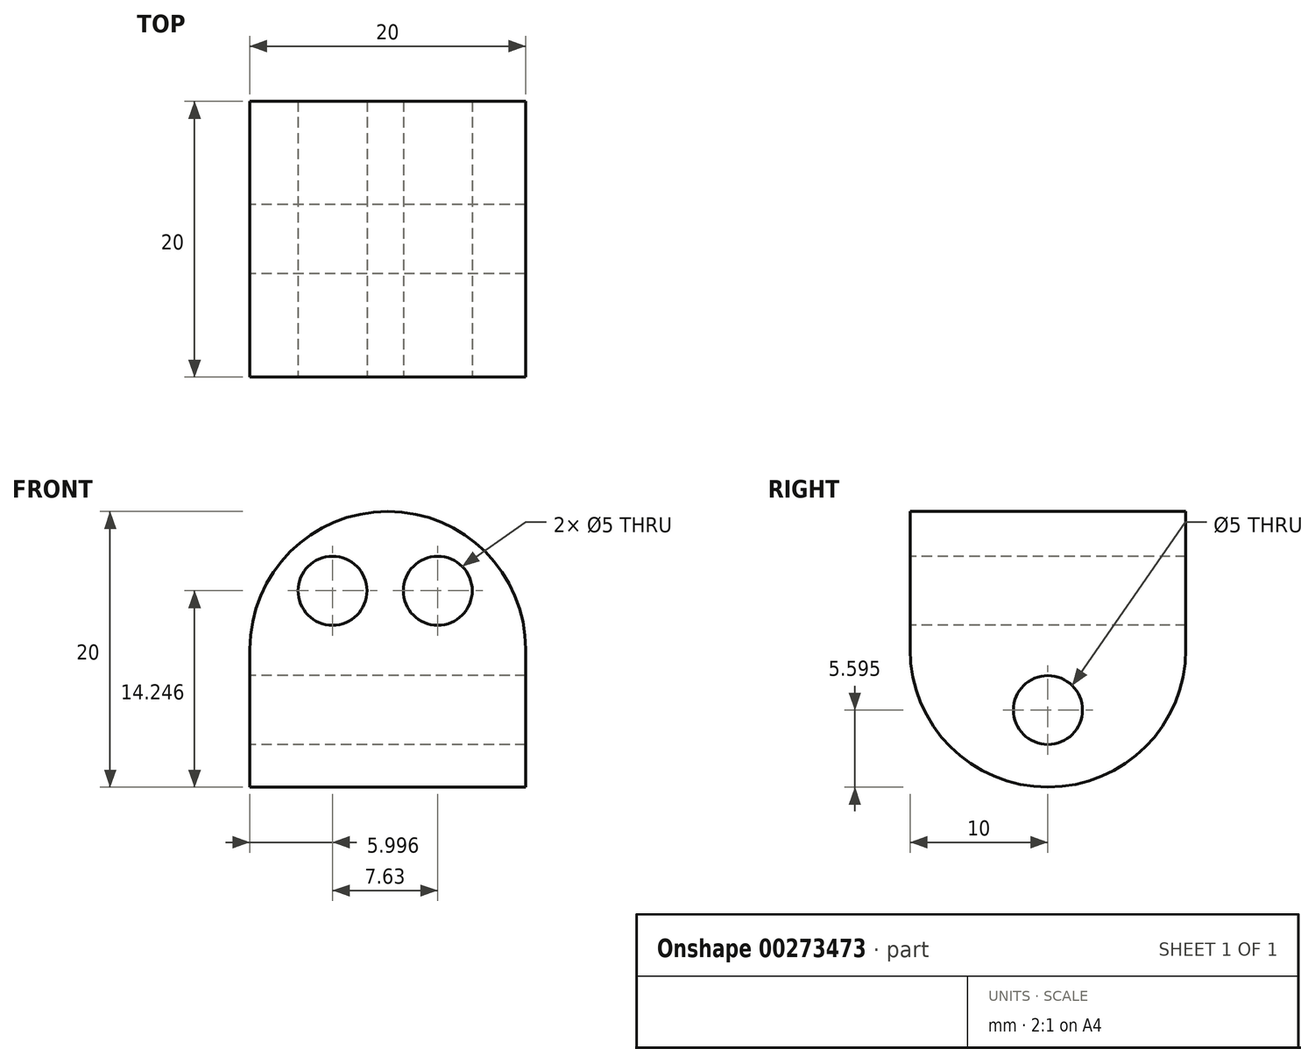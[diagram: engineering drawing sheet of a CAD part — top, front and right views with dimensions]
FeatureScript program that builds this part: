
annotation { "Feature Type Name" : "Feature", "Feature Type Description" : "" }
export const myFeature = defineFeature(function(context is Context, id is Id, definition is map)
    precondition{}
    {
        {
            var Q0;
            Q0=qCreatedBy(makeId("Top.planeOp"),FACE);
            var sketch = newSketch(context, id + "F0", { "sketchPlane" : qUnion([Q0])});
            skLineSegment(sketch, "E0.bottom", {"start": v(10, 10) * mm, "end": v(-10, 10) * mm});
            skLineSegment(sketch, "E0.top", {"start": v(10, -10) * mm, "end": v(-10, -10) * mm});
            skLineSegment(sketch, "E0.left", {"start": v(10, 10) * mm, "end": v(10, -10) * mm});
            skLineSegment(sketch, "E0.right", {"start": v(-10, 10) * mm, "end": v(-10, -10) * mm});
            skPoint(sketch, "E0.middle", {"position": v(0, 0) * mm});
            skSolve(sketch);
        }
        {
            var Q0;
            Q0=makeQuery(id+"F0.imprint","IMPRINT",FACE,{"disambiguationData":[TD([[makeQuery(id+"F0.imprint","IMPRINT",EDGE,{"derivedFrom":sQuery(id+"F0.wireOp",EDGE,"E0.bottom")}),1.0]])]});
            extrude(context, id + "F1", {"entities" : qUnion([Q0]), "depth" : 20 * mm});
        }
        {
            var Q0;
            Q0=makeQuery(id+"F1.opExtrude","CAP_EDGE",EDGE,{"disambiguationData":[OSD([sQuery(id+"F0.wireOp",EDGE,"E0.left")])],"isStart":false});
            var Q1;
            Q1=makeQuery(id+"F1.opExtrude","CAP_EDGE",EDGE,{"disambiguationData":[OSD([sQuery(id+"F0.wireOp",EDGE,"E0.right")])],"isStart":false});
            var Q2;
            Q2=makeQuery(id+"F1.opExtrude","CAP_EDGE",EDGE,{"disambiguationData":[OSD([sQuery(id+"F0.wireOp",EDGE,"E0.top")])],"isStart":true});
            var Q3;
            Q3=makeQuery(id+"F1.opExtrude","CAP_EDGE",EDGE,{"disambiguationData":[OSD([sQuery(id+"F0.wireOp",EDGE,"E0.bottom")])],"isStart":true});
            fillet(context, id + "F2", {"entities" : qUnion([Q0, Q1, Q2, Q3]), "radius" : 10 * mm, "tangentPropagation" : true, "allowEdgeOverflow" : false});
        }
        {
            var Q0;
            Q0=makeQuery(id+"F1.opExtrude","SWEPT_FACE",FACE,{"disambiguationData":[OSD([sQuery(id+"F0.wireOp",EDGE,"E0.top")])]});
            var sketch = newSketch(context, id + "F3", { "sketchPlane" : qUnion([Q0])});
            skPoint(sketch, "E1", {"position": v(-4, 14.25) * mm});
            skPoint(sketch, "E2", {"position": v(3.63, 14.25) * mm});
            skSolve(sketch);
        }
        {
            var Q0;
            Q0=makeQuery(id+"F1.opExtrude","SWEPT_FACE",FACE,{"disambiguationData":[OSD([sQuery(id+"F0.wireOp",EDGE,"E0.right")])]});
            var sketch = newSketch(context, id + "F4", { "sketchPlane" : qUnion([Q0])});
            skPoint(sketch, "E3", {"position": v(0, 5.6) * mm});
            skSolve(sketch);
        }
        {
            var Q0;
            Q0=sQuery(id+"F4.wireOp",VERTEX,"E3");
            var Q1;
            Q1=makeQuery(id+"F1.opExtrude","SWEPT_BODY",BODY,{"disambiguationData":[OSD([sQuery(id+"F0.wireOp",EDGE,"E0.bottom"),sQuery(id+"F0.wireOp",EDGE,"E0.top"),sQuery(id+"F0.wireOp",EDGE,"E0.left"),sQuery(id+"F0.wireOp",EDGE,"E0.right")])]});
            hole(context, id + "F5", {"style" : HoleStyle.SIMPLE, "endStyle" : HoleEndStyle.THROUGH, "holeDiameter" : 5 * mm, "tappedDepth" : 12 * mm, "tapClearance" : 3, "locations" : qUnion([Q0]), "scope" : qUnion([Q1])});
        }
        {
            var Q0;
            Q0=sQuery(id+"F3.wireOp",VERTEX,"E1");
            var Q1;
            Q1=sQuery(id+"F3.wireOp",VERTEX,"E2");
            var Q2;
            Q2=makeQuery(id+"F1.opExtrude","SWEPT_BODY",BODY,{"disambiguationData":[OSD([sQuery(id+"F0.wireOp",EDGE,"E0.bottom"),sQuery(id+"F0.wireOp",EDGE,"E0.top"),sQuery(id+"F0.wireOp",EDGE,"E0.left"),sQuery(id+"F0.wireOp",EDGE,"E0.right")])]});
            hole(context, id + "F6", {"style" : HoleStyle.SIMPLE, "endStyle" : HoleEndStyle.THROUGH, "holeDiameter" : 5 * mm, "tappedDepth" : 12 * mm, "tapClearance" : 3, "locations" : qUnion([Q0, Q1]), "scope" : qUnion([Q2])});
        }
    });
